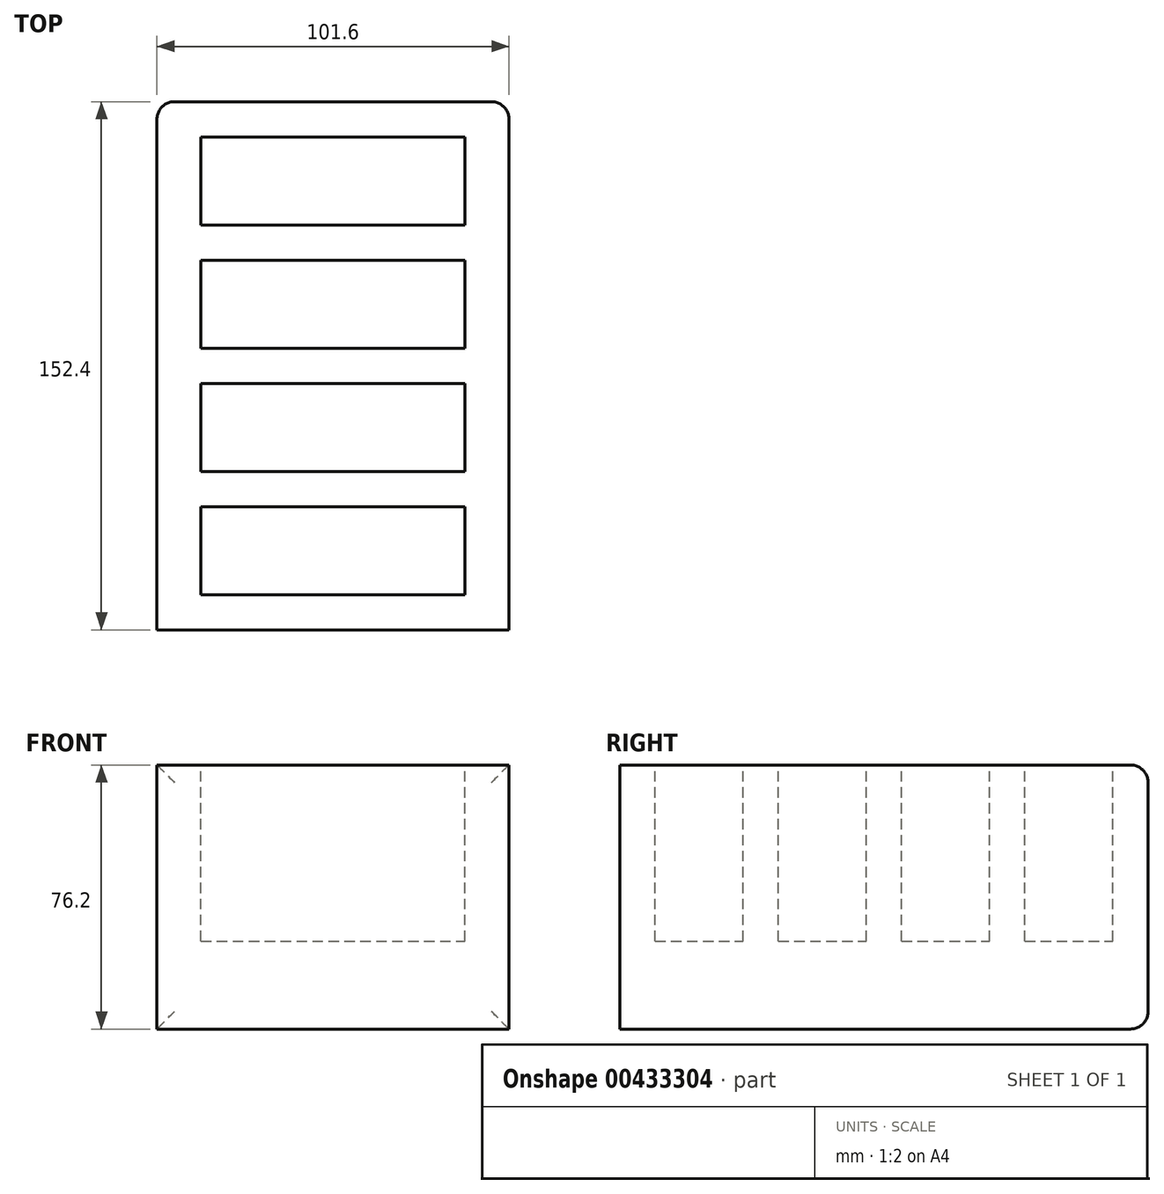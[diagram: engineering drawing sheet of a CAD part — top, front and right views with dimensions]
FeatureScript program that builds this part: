
annotation { "Feature Type Name" : "Feature", "Feature Type Description" : "" }
export const myFeature = defineFeature(function(context is Context, id is Id, definition is map)
    precondition{}
    {
        {
            var Q0;
            Q0=qCreatedBy(makeId("Front.planeOp"),FACE);
            var sketch = newSketch(context, id + "F0", { "sketchPlane" : qUnion([Q0])});
            skLineSegment(sketch, "E0.bottom", {"start": v(-40.41, 17.15) * mm, "end": v(61.19, 17.15) * mm});
            skLineSegment(sketch, "E0.top", {"start": v(-40.41, -59.05) * mm, "end": v(61.19, -59.05) * mm});
            skLineSegment(sketch, "E0.left", {"start": v(-40.41, 17.15) * mm, "end": v(-40.41, -59.05) * mm});
            skLineSegment(sketch, "E0.right", {"start": v(61.19, 17.15) * mm, "end": v(61.19, -59.05) * mm});
            skSolve(sketch);
        }
        {
            var Q0;
            Q0=makeQuery(id+"F0.imprint","IMPRINT",FACE,{"disambiguationData":[TD([[makeQuery(id+"F0.imprint","IMPRINT",EDGE,{"derivedFrom":sQuery(id+"F0.wireOp",EDGE,"E0.bottom")}),-1.0]])]});
            extrude(context, id + "F1", {"entities" : qUnion([Q0]), "depth" : 152.4 * mm});
        }
        {
            var Q0;
            Q0=makeQuery(id+"F1.opExtrude","SWEPT_FACE",FACE,{"disambiguationData":[OSD([sQuery(id+"F0.wireOp",EDGE,"E0.bottom")])]});
            var sketch = newSketch(context, id + "F2", { "sketchPlane" : qUnion([Q0])});
            skLineSegment(sketch, "E1.bottom", {"start": v(-27.71, -142.24) * mm, "end": v(48.49, -142.24) * mm});
            skLineSegment(sketch, "E1.top", {"start": v(-27.71, -116.84) * mm, "end": v(48.49, -116.84) * mm});
            skLineSegment(sketch, "E1.left", {"start": v(-27.71, -142.24) * mm, "end": v(-27.71, -116.84) * mm});
            skLineSegment(sketch, "E1.right", {"start": v(48.49, -142.24) * mm, "end": v(48.49, -116.84) * mm});
            skLineSegment(sketch, "E2.0.1.0", {"start": v(-27.71, -81.28) * mm, "end": v(48.49, -81.28) * mm});
            skLineSegment(sketch, "E2.0.1.1", {"start": v(-27.71, -106.68) * mm, "end": v(-27.71, -81.28) * mm});
            skLineSegment(sketch, "E2.0.1.2", {"start": v(-27.71, -106.68) * mm, "end": v(48.49, -106.68) * mm});
            skLineSegment(sketch, "E2.0.1.3", {"start": v(48.49, -106.68) * mm, "end": v(48.49, -81.28) * mm});
            skLineSegment(sketch, "E2.0.2.0", {"start": v(-27.71, -45.72) * mm, "end": v(48.49, -45.72) * mm});
            skLineSegment(sketch, "E2.0.2.1", {"start": v(-27.71, -71.12) * mm, "end": v(-27.71, -45.72) * mm});
            skLineSegment(sketch, "E2.0.2.2", {"start": v(-27.71, -71.12) * mm, "end": v(48.49, -71.12) * mm});
            skLineSegment(sketch, "E2.0.2.3", {"start": v(48.49, -71.12) * mm, "end": v(48.49, -45.72) * mm});
            skLineSegment(sketch, "E2.0.3.0", {"start": v(-27.71, -10.16) * mm, "end": v(48.49, -10.16) * mm});
            skLineSegment(sketch, "E2.0.3.1", {"start": v(-27.71, -35.56) * mm, "end": v(-27.71, -10.16) * mm});
            skLineSegment(sketch, "E2.0.3.2", {"start": v(-27.71, -35.56) * mm, "end": v(48.49, -35.56) * mm});
            skLineSegment(sketch, "E2.0.3.3", {"start": v(48.49, -35.56) * mm, "end": v(48.49, -10.16) * mm});
            skLineSegment(sketch, "E2.direction1", {"start": v(-27.71, -116.84) * mm, "end": v(39.6, -116.84) * mm, "construction": true});
            skLineSegment(sketch, "E2.direction2", {"start": v(-27.71, -116.84) * mm, "end": v(-27.71, -81.28) * mm, "construction": true});
            skSolve(sketch);
        }
        {
            var Q0;
            Q0=makeQuery(id+"F2.imprint","IMPRINT",FACE,{"disambiguationData":[TD([[makeQuery(id+"F2.imprint","IMPRINT",EDGE,{"derivedFrom":sQuery(id+"F2.wireOp",EDGE,"E2.0.3.0")}),-1.0]])]});
            var Q1;
            Q1=makeQuery(id+"F2.imprint","IMPRINT",FACE,{"disambiguationData":[TD([[makeQuery(id+"F2.imprint","IMPRINT",EDGE,{"derivedFrom":sQuery(id+"F2.wireOp",EDGE,"E2.0.2.0")}),-1.0]])]});
            var Q2;
            Q2=makeQuery(id+"F2.imprint","IMPRINT",FACE,{"disambiguationData":[TD([[makeQuery(id+"F2.imprint","IMPRINT",EDGE,{"derivedFrom":sQuery(id+"F2.wireOp",EDGE,"E2.0.1.0")}),-1.0]])]});
            var Q3;
            Q3=makeQuery(id+"F2.imprint","IMPRINT",FACE,{"disambiguationData":[TD([[makeQuery(id+"F2.imprint","IMPRINT",EDGE,{"derivedFrom":sQuery(id+"F2.wireOp",EDGE,"E1.bottom")}),1.0]])]});
            extrude(context, id + "F3", {"entities" : qUnion([Q0, Q1, Q2, Q3]), "operationType" : NewBodyOperationType.REMOVE, "oppositeDirection" : true, "depth" : 50.8 * mm});
        }
        {
            var Q0;
            Q0=makeQuery(id+"F1.opExtrude","CAP_EDGE",EDGE,{"disambiguationData":[OSD([sQuery(id+"F0.wireOp",EDGE,"E0.right")])],"isStart":true});
            var Q1;
            Q1=makeQuery(id+"F1.opExtrude","CAP_EDGE",EDGE,{"disambiguationData":[OSD([sQuery(id+"F0.wireOp",EDGE,"E0.top")])],"isStart":true});
            var Q2;
            Q2=makeQuery(id+"F1.opExtrude","CAP_EDGE",EDGE,{"disambiguationData":[OSD([sQuery(id+"F0.wireOp",EDGE,"E0.bottom")])],"isStart":true});
            var Q3;
            Q3=makeQuery(id+"F1.opExtrude","CAP_EDGE",EDGE,{"disambiguationData":[OSD([sQuery(id+"F0.wireOp",EDGE,"E0.left")])],"isStart":true});
            fillet(context, id + "F4", {"entities" : qUnion([Q0, Q1, Q2, Q3]), "radius" : 5.08 * mm, "tangentPropagation" : true, "allowEdgeOverflow" : false});
        }
    });
